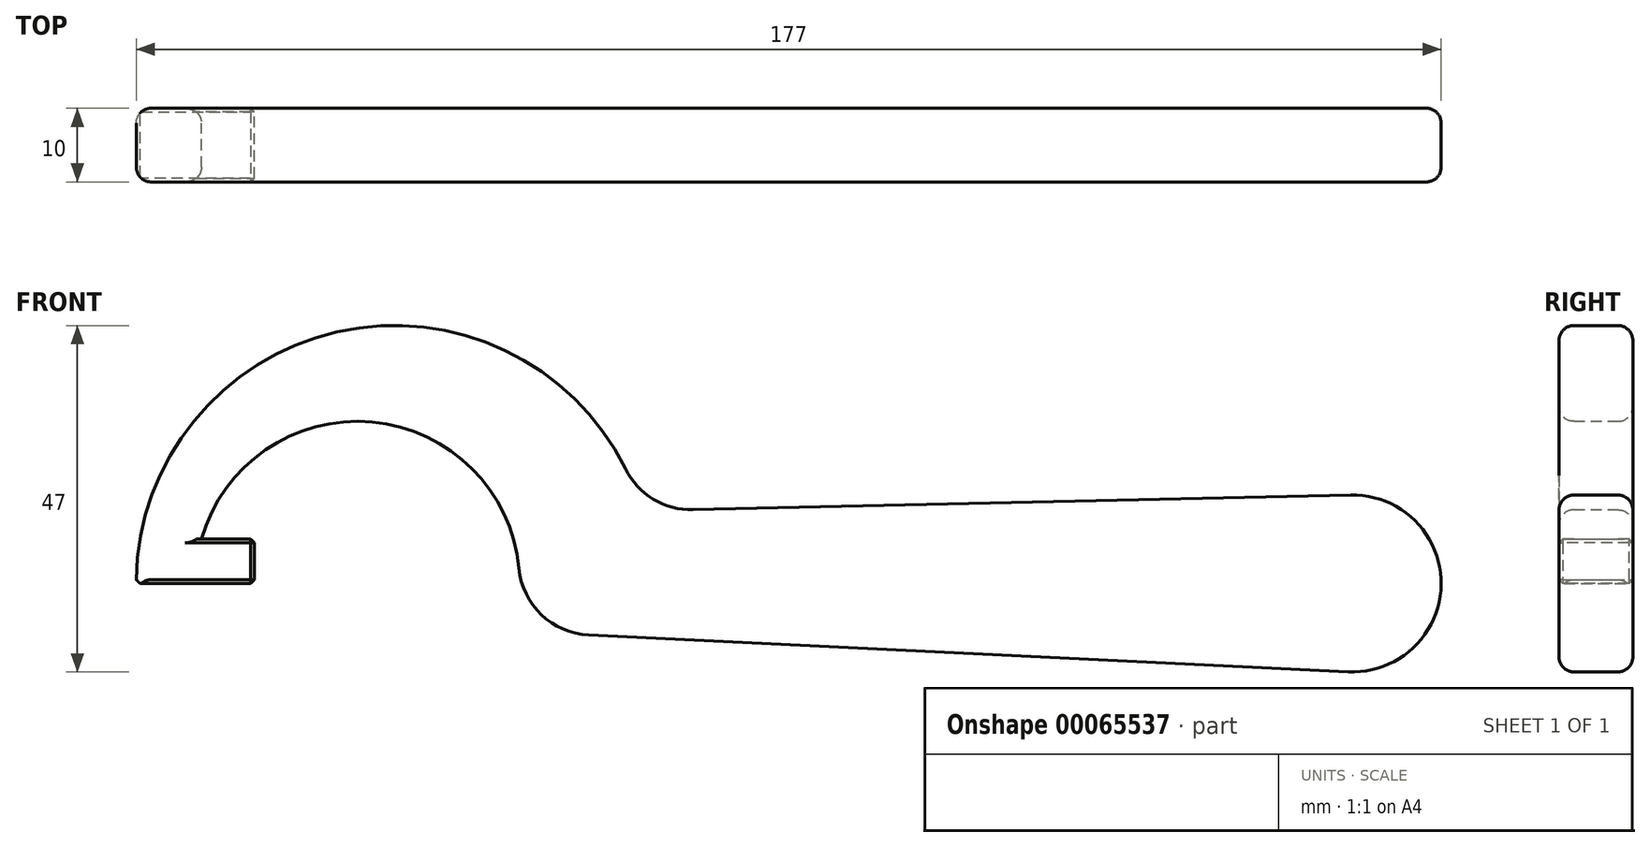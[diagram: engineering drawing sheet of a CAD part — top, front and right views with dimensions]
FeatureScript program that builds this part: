
annotation { "Feature Type Name" : "Feature", "Feature Type Description" : "" }
export const myFeature = defineFeature(function(context is Context, id is Id, definition is map)
    precondition{}
    {
        {
            var Q0;
            Q0=qCreatedBy(makeId("Front.planeOp"),FACE);
            var sketch = newSketch(context, id + "F0", { "sketchPlane" : qUnion([Q0])});
            skArc(sketch, "E0", {"start": v(21.9, 2.06) * mm, "mid": v(2, 21.9) * mm, "end": v(-21.17, 6) * mm});
            skArc(sketch, "E1", {"start": v(36.35, 15.56) * mm, "mid": v(-2.99, 34.08) * mm, "end": v(-30, 0) * mm});
            skArc(sketch, "E2", {"start": v(134.42, -11.99) * mm, "mid": v(147, -0.16) * mm, "end": v(134.73, 12) * mm});
            skLineSegment(sketch, "E3", {"start": v(-30, 0) * mm, "end": v(-14, 0) * mm});
            skLineSegment(sketch, "E4", {"start": v(-14, 0) * mm, "end": v(-14, 6) * mm});
            skLineSegment(sketch, "E5", {"start": v(-14, 6) * mm, "end": v(-21.17, 6) * mm});
            skArc(sketch, "E6", {"start": v(36.35, 15.56) * mm, "mid": v(40.14, 11.44) * mm, "end": v(45.53, 10) * mm});
            skLineSegment(sketch, "E7", {"start": v(134.73, 12) * mm, "end": v(45.53, 10) * mm});
            skArc(sketch, "E8", {"start": v(21.9, 2.06) * mm, "mid": v(24.95, -4.23) * mm, "end": v(31.37, -6.99) * mm});
            skLineSegment(sketch, "E9", {"start": v(134.42, -11.99) * mm, "end": v(31.37, -6.99) * mm});
            skSolve(sketch);
        }
        {
            var Q0;
            Q0=makeQuery(id+"F0.imprint","IMPRINT",FACE,{"disambiguationData":[TD([[makeQuery(id+"F0.imprint","IMPRINT",EDGE,{"derivedFrom":sQuery(id+"F0.wireOp",EDGE,"E0")}),-1.0]])]});
            extrude(context, id + "F1", {"entities" : qUnion([Q0]), "depth" : 10 * mm});
        }
        {
            var Q0;
            Q0=makeQuery(id+"F1.opExtrude","CAP_EDGE",EDGE,{"disambiguationData":[OSD([sQuery(id+"F0.wireOp",EDGE,"E3")])],"isStart":false});
            var Q1;
            Q1=makeQuery(id+"F1.opExtrude","CAP_EDGE",EDGE,{"disambiguationData":[OSD([sQuery(id+"F0.wireOp",EDGE,"E4")])],"isStart":false});
            var Q2;
            Q2=makeQuery(id+"F1.opExtrude","CAP_EDGE",EDGE,{"disambiguationData":[OSD([sQuery(id+"F0.wireOp",EDGE,"E5")])],"isStart":false});
            var Q3;
            Q3=makeQuery(id+"F1.opExtrude","CAP_EDGE",EDGE,{"disambiguationData":[OSD([sQuery(id+"F0.wireOp",EDGE,"E4")])],"isStart":true});
            var Q4;
            Q4=makeQuery(id+"F1.opExtrude","SWEPT_EDGE",EDGE,{"disambiguationData":[OSD([sQuery(id+"F0.wireOp",EDGE,"E4"),sQuery(id+"F0.wireOp",EDGE,"E5")])]});
            var Q5;
            Q5=makeQuery(id+"F1.opExtrude","SWEPT_EDGE",EDGE,{"disambiguationData":[OSD([sQuery(id+"F0.wireOp",EDGE,"E3"),sQuery(id+"F0.wireOp",EDGE,"E4")])]});
            var Q6;
            Q6=makeQuery(id+"F1.opExtrude","CAP_EDGE",EDGE,{"disambiguationData":[OSD([sQuery(id+"F0.wireOp",EDGE,"E5")])],"isStart":true});
            var Q7;
            Q7=makeQuery(id+"F1.opExtrude","CAP_EDGE",EDGE,{"disambiguationData":[OSD([sQuery(id+"F0.wireOp",EDGE,"E3")])],"isStart":true});
            var Q8;
            Q8=makeQuery(id+"F1.opExtrude","SWEPT_EDGE",EDGE,{"disambiguationData":[OSD([sQuery(id+"F0.wireOp",EDGE,"E1"),sQuery(id+"F0.wireOp",EDGE,"E3")])]});
            chamfer(context, id + "F2", {"entities" : qUnion([Q0, Q1, Q2, Q3, Q4, Q5, Q6, Q7, Q8]), "width" : 0.5 * mm, "tangentPropagation" : true});
        }
        {
            var Q0;
            Q0=makeQuery(id+"F1.opExtrude","CAP_EDGE",EDGE,{"disambiguationData":[OSD([sQuery(id+"F0.wireOp",EDGE,"E1")])],"isStart":false});
            var Q1;
            Q1=makeQuery(id+"F1.opExtrude","CAP_EDGE",EDGE,{"disambiguationData":[OSD([sQuery(id+"F0.wireOp",EDGE,"E1")])],"isStart":true});
            var Q2;
            Q2=makeQuery(id+"F1.opExtrude","CAP_EDGE",EDGE,{"disambiguationData":[OSD([sQuery(id+"F0.wireOp",EDGE,"E6")])],"isStart":false});
            var Q3;
            Q3=makeQuery(id+"F1.opExtrude","CAP_EDGE",EDGE,{"disambiguationData":[OSD([sQuery(id+"F0.wireOp",EDGE,"E7")])],"isStart":false});
            var Q4;
            Q4=makeQuery(id+"F1.opExtrude","CAP_EDGE",EDGE,{"disambiguationData":[OSD([sQuery(id+"F0.wireOp",EDGE,"E2")])],"isStart":false});
            var Q5;
            Q5=makeQuery(id+"F1.opExtrude","CAP_EDGE",EDGE,{"disambiguationData":[OSD([sQuery(id+"F0.wireOp",EDGE,"E9")])],"isStart":false});
            var Q6;
            Q6=makeQuery(id+"F1.opExtrude","CAP_EDGE",EDGE,{"disambiguationData":[OSD([sQuery(id+"F0.wireOp",EDGE,"E8")])],"isStart":false});
            var Q7;
            Q7=makeQuery(id+"F1.opExtrude","CAP_EDGE",EDGE,{"disambiguationData":[OSD([sQuery(id+"F0.wireOp",EDGE,"E0")])],"isStart":false});
            var Q8;
            Q8=makeQuery(id+"F1.opExtrude","CAP_EDGE",EDGE,{"disambiguationData":[OSD([sQuery(id+"F0.wireOp",EDGE,"E6")])],"isStart":true});
            var Q9;
            Q9=makeQuery(id+"F1.opExtrude","CAP_EDGE",EDGE,{"disambiguationData":[OSD([sQuery(id+"F0.wireOp",EDGE,"E7")])],"isStart":true});
            var Q10;
            Q10=makeQuery(id+"F1.opExtrude","CAP_EDGE",EDGE,{"disambiguationData":[OSD([sQuery(id+"F0.wireOp",EDGE,"E2")])],"isStart":true});
            var Q11;
            Q11=makeQuery(id+"F1.opExtrude","CAP_EDGE",EDGE,{"disambiguationData":[OSD([sQuery(id+"F0.wireOp",EDGE,"E0")])],"isStart":true});
            var Q12;
            Q12=makeQuery(id+"F1.opExtrude","CAP_EDGE",EDGE,{"disambiguationData":[OSD([sQuery(id+"F0.wireOp",EDGE,"E8")])],"isStart":true});
            var Q13;
            Q13=makeQuery(id+"F1.opExtrude","CAP_EDGE",EDGE,{"disambiguationData":[OSD([sQuery(id+"F0.wireOp",EDGE,"E9")])],"isStart":true});
            fillet(context, id + "F3", {"entities" : qUnion([Q0, Q1, Q2, Q3, Q4, Q5, Q6, Q7, Q8, Q9, Q10, Q11, Q12, Q13]), "radius" : 2 * mm, "tangentPropagation" : true, "allowEdgeOverflow" : false});
        }
    });
